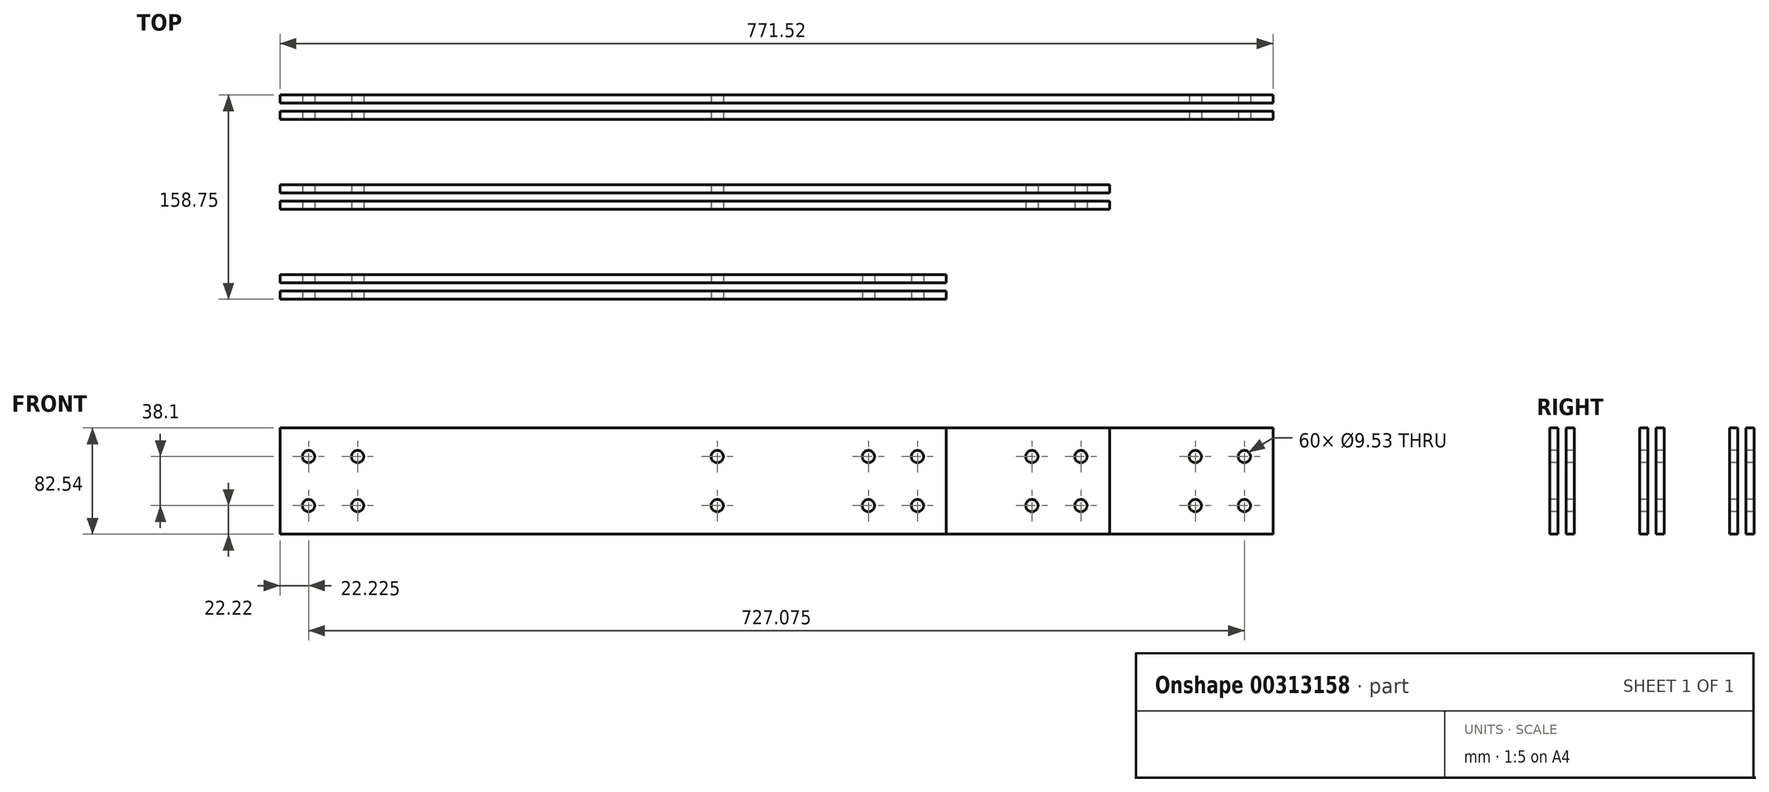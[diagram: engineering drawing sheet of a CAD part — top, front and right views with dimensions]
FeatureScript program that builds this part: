
annotation { "Feature Type Name" : "Feature", "Feature Type Description" : "" }
export const myFeature = defineFeature(function(context is Context, id is Id, definition is map)
    precondition{}
    {
        {
            var Q0;
            Q0=qCreatedBy(makeId("Top.planeOp"),FACE);
            var sketch = newSketch(context, id + "F0", { "sketchPlane" : qUnion([Q0])});
            skLineSegment(sketch, "E0.bottom", {"start": v(0, 0) * mm, "end": v(771.53, 0) * mm});
            skLineSegment(sketch, "E0.top", {"start": v(0, -6.35) * mm, "end": v(771.53, -6.35) * mm});
            skLineSegment(sketch, "E0.left", {"start": v(0, 0) * mm, "end": v(0, -6.35) * mm});
            skLineSegment(sketch, "E0.right", {"start": v(771.53, 0) * mm, "end": v(771.53, -6.35) * mm});
            skLineSegment(sketch, "E1.bottom", {"start": v(771.53, -12.7) * mm, "end": v(0, -12.7) * mm});
            skLineSegment(sketch, "E1.top", {"start": v(771.53, -19.05) * mm, "end": v(0, -19.05) * mm});
            skLineSegment(sketch, "E1.left", {"start": v(771.53, -12.7) * mm, "end": v(771.53, -19.05) * mm});
            skLineSegment(sketch, "E1.right", {"start": v(0, -12.7) * mm, "end": v(0, -19.05) * mm});
            skLineSegment(sketch, "E2.bottom", {"start": v(0, -69.85) * mm, "end": v(644.53, -69.85) * mm});
            skLineSegment(sketch, "E2.top", {"start": v(0, -76.2) * mm, "end": v(644.53, -76.2) * mm});
            skLineSegment(sketch, "E2.left", {"start": v(0, -69.85) * mm, "end": v(0, -76.2) * mm});
            skLineSegment(sketch, "E2.right", {"start": v(644.53, -69.85) * mm, "end": v(644.53, -76.2) * mm});
            skLineSegment(sketch, "E3.bottom", {"start": v(644.53, -82.55) * mm, "end": v(0, -82.55) * mm});
            skLineSegment(sketch, "E3.top", {"start": v(644.53, -88.9) * mm, "end": v(0, -88.9) * mm});
            skLineSegment(sketch, "E3.left", {"start": v(644.53, -82.55) * mm, "end": v(644.53, -88.9) * mm});
            skLineSegment(sketch, "E3.right", {"start": v(0, -82.55) * mm, "end": v(0, -88.9) * mm});
            skLineSegment(sketch, "E4.bottom", {"start": v(0, -139.7) * mm, "end": v(517.53, -139.7) * mm});
            skLineSegment(sketch, "E4.top", {"start": v(0, -146.05) * mm, "end": v(517.53, -146.05) * mm});
            skLineSegment(sketch, "E4.left", {"start": v(0, -139.7) * mm, "end": v(0, -146.05) * mm});
            skLineSegment(sketch, "E4.right", {"start": v(517.53, -139.7) * mm, "end": v(517.53, -146.05) * mm});
            skLineSegment(sketch, "E5.bottom", {"start": v(517.53, -152.4) * mm, "end": v(0, -152.4) * mm});
            skLineSegment(sketch, "E5.top", {"start": v(517.53, -158.75) * mm, "end": v(0, -158.75) * mm});
            skLineSegment(sketch, "E5.left", {"start": v(517.53, -152.4) * mm, "end": v(517.53, -158.75) * mm});
            skLineSegment(sketch, "E5.right", {"start": v(0, -152.4) * mm, "end": v(0, -158.75) * mm});
            skSolve(sketch);
        }
        {
            var Q0;
            Q0 = qSketchRegion(id + "F0", true);
            extrude(context, id + "F1", {"entities" : qUnion([Q0]), "endBound" : BoundingType.SYMMETRIC, "depth" : 82.55 * mm});
        }
        {
            var Q0;
            Q0=makeQuery(id+"F1.opExtrude","SWEPT_FACE",FACE,{"disambiguationData":[OSD([sQuery(id+"F0.wireOp",EDGE,"E5.top")])]});
            var sketch = newSketch(context, id + "F2", { "sketchPlane" : qUnion([Q0])});
            skCircle(sketch, "E6", {"center": v(22.22, 19.05) * mm, "radius": 4.76 * mm});
            skCircle(sketch, "E7", {"center": v(22.22, -19.05) * mm, "radius": 4.76 * mm});
            skCircle(sketch, "E8", {"center": v(60.32, -19.05) * mm, "radius": 4.76 * mm});
            skCircle(sketch, "E9", {"center": v(60.32, 19.05) * mm, "radius": 4.76 * mm});
            skCircle(sketch, "E10", {"center": v(339.73, 19.05) * mm, "radius": 4.76 * mm});
            skCircle(sketch, "E11", {"center": v(339.73, -19.05) * mm, "radius": 4.76 * mm});
            skSolve(sketch);
        }
        {
            var Q0;
            Q0 = qSketchRegion(id + "F2", true);
            extrude(context, id + "F3", {"entities" : qUnion([Q0]), "operationType" : NewBodyOperationType.REMOVE, "endBound" : BoundingType.THROUGH_ALL, "oppositeDirection" : true, "depth" : 25.4 * mm});
        }
        {
            var Q0;
            Q0=makeQuery(id+"F1.opExtrude","SWEPT_FACE",FACE,{"disambiguationData":[OSD([sQuery(id+"F0.wireOp",EDGE,"E5.top")])]});
            var sketch = newSketch(context, id + "F4", { "sketchPlane" : qUnion([Q0])});
            skCircle(sketch, "E12", {"center": v(457.2, 19.05) * mm, "radius": 4.76 * mm});
            skCircle(sketch, "E13", {"center": v(457.2, -19.05) * mm, "radius": 4.76 * mm});
            skCircle(sketch, "E14", {"center": v(495.3, -19.05) * mm, "radius": 4.76 * mm});
            skCircle(sketch, "E15", {"center": v(495.3, 19.05) * mm, "radius": 4.76 * mm});
            skSolve(sketch);
        }
        {
            var Q0;
            Q0 = qSketchRegion(id + "F4", true);
            var Q1;
            Q1=makeQuery(id+"F1.opExtrude","SWEPT_FACE",FACE,{"disambiguationData":[OSD([sQuery(id+"F0.wireOp",EDGE,"E4.bottom")])]});
            extrude(context, id + "F5", {"entities" : qUnion([Q0]), "operationType" : NewBodyOperationType.REMOVE, "endBound" : BoundingType.UP_TO_SURFACE, "oppositeDirection" : true, "endBoundEntityFace" : qUnion([Q1]), "depth" : 25.4 * mm});
        }
        {
            var Q0;
            Q0=makeQuery(id+"F1.opExtrude","SWEPT_FACE",FACE,{"disambiguationData":[OSD([sQuery(id+"F0.wireOp",EDGE,"E3.top")])]});
            var sketch = newSketch(context, id + "F6", { "sketchPlane" : qUnion([Q0])});
            skCircle(sketch, "E16", {"center": v(584.2, 19.05) * mm, "radius": 4.76 * mm});
            skCircle(sketch, "E17", {"center": v(584.2, -19.05) * mm, "radius": 4.76 * mm});
            skCircle(sketch, "E18", {"center": v(622.3, -19.05) * mm, "radius": 4.76 * mm});
            skCircle(sketch, "E19", {"center": v(622.3, 19.05) * mm, "radius": 4.76 * mm});
            skSolve(sketch);
        }
        {
            var Q0;
            Q0 = qSketchRegion(id + "F6", true);
            var Q1;
            Q1=makeQuery(id+"F1.opExtrude","SWEPT_FACE",FACE,{"disambiguationData":[OSD([sQuery(id+"F0.wireOp",EDGE,"E2.bottom")])]});
            extrude(context, id + "F7", {"entities" : qUnion([Q0]), "operationType" : NewBodyOperationType.REMOVE, "endBound" : BoundingType.UP_TO_SURFACE, "oppositeDirection" : true, "endBoundEntityFace" : qUnion([Q1]), "depth" : 25.4 * mm});
        }
        {
            var Q0;
            Q0=makeQuery(id+"F1.opExtrude","SWEPT_FACE",FACE,{"disambiguationData":[OSD([sQuery(id+"F0.wireOp",EDGE,"E1.top")])]});
            var sketch = newSketch(context, id + "F8", { "sketchPlane" : qUnion([Q0])});
            skCircle(sketch, "E20", {"center": v(711.2, 19.05) * mm, "radius": 4.76 * mm});
            skCircle(sketch, "E21", {"center": v(711.2, -19.05) * mm, "radius": 4.76 * mm});
            skCircle(sketch, "E22", {"center": v(749.3, -19.05) * mm, "radius": 4.76 * mm});
            skCircle(sketch, "E23", {"center": v(749.3, 19.05) * mm, "radius": 4.76 * mm});
            skSolve(sketch);
        }
        {
            var Q0;
            Q0 = qSketchRegion(id + "F8", true);
            var Q1;
            Q1=makeQuery(id+"F1.opExtrude","SWEPT_FACE",FACE,{"disambiguationData":[OSD([sQuery(id+"F0.wireOp",EDGE,"E0.bottom")])]});
            extrude(context, id + "F9", {"entities" : qUnion([Q0]), "operationType" : NewBodyOperationType.REMOVE, "endBound" : BoundingType.UP_TO_SURFACE, "oppositeDirection" : true, "endBoundEntityFace" : qUnion([Q1]), "depth" : 25.4 * mm});
        }
    });
